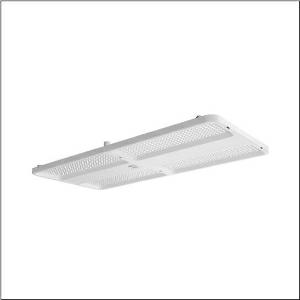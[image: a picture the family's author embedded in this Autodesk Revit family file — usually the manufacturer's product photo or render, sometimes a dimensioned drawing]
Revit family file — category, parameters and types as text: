
# Revit family: highbay_21_maxi_52hn12db4mda01
name_source: partatom
category: Lighting Fixtures
units: mm (PartAtom-declared; Revit-internal decimal feet)

## family parameters
Cut with Voids When Loaded = No
Host = Face
Light Source = No
Part Type = Normal
Room Calculation Point = No
Round Connector Dimension = Use Diameter
Shared = No

## types (1)
- --- (1 x LED, 28000 lm, 144.5 W, 4000K)
    Apparent Load = 144 VA
    CIE Flux Codes = 90 98 100 100 100
    Color Rendering = 80
    Color Temperature = 4000K
    Default Elevation = 1800 mm
    Description = high bay luminaire Highbay 21 maxi; direct symmetric wide distribution, light control with lens of PMMA; UGR ≤ 22 (X = 4H | Y = 8H | S = 0.25H | reflection values 70/50/20); luminous flux: 28.000lm; light colour: 840, colour temperature: 4000K, MacAdam ≤ 3 SDCM (initial), colour rendering: CRI > 80; luminous efficacy: 193,8lm/W; rated service life: 75.000h (L80) at AT= ta max; control: Bluetooth Mesh; for wireless networking: Node multi-sensor luminaire for setting up a local control solution without a higher-level application controller, intelligence completely integrated into the luminaire; with auto-swarm function: leading lighting creates safety. The function is already active without any „out-of-the-box“ commissioning; commissioning is not necessary thanks to „out-of-the-box“ functions: basic functions (presence lighting, follow-up times, fading times, etc.) are already preset at the factory; no control line such as DALI between the Node multi-sensor luminaires and Nodes is required, wireless integration of other Node luminaires and Node multi-sensor luminaires into the network is possible; number of Node multi-sensor luminaires in the project can be expanded as required, network sizes > 300 Nodes can be realized; can also be connected to lighting or building automation via various gateways upon request; integrated DALI2 ECG provides luminaire data (according to IEC62386, Part 251), energy data (Part 252), and monitoring and analytics data (Part 253) to higher-level systems for further processing; luminaire with PIR sensor (passive-infrared); with light sensor; luminaire connection: terminal, 5-pole, max. 2.5mm² (cable entry for one cable, Ø 8.5..16mm); mains connection: 230..240V, AC 50/60Hz; connected load: 144,5W; protection rating (complete): IP65; insulation class (complete): insulation class I (protective earthing); protection symbol: D; certification: CE, UKCA; internal wiring halogen-free; luminaire LABS conformity tested according to VDMA 24364:2018-05; Suitable for use in the food industry according to the specifications of IFS-Food, HACCP and/or BRC; housing frame of high-performance plastic PA6, matt traffic white (RAL 9016); cover of PMMA; dimension (LxWxH): 946 x 442 x 72mm; permissible operating ambient temperature: -20..+45°C (reducing of maximum allowable ambient temperature of 5°C with ceiling mounting); packaging unit: 1 piece; (delivery without accessories; please order mounting accessories separately)
    Height = 72 mm  [stored 0.23622 ft]
    Lamp = 1 x LED
    Lamp Light Flux = 28000 lm
    Lamp Power = 144.5 W
    Lamp count = 1
    Length = 946 mm
    Luminous efficacy = 194 lm/W
    Manufacturer = Siteco
    ModVariant = No
    Model = 52HN12DB4MDA01
    Mounting Place = Ceiling
    Mounting Type = Pendant
    Number of Poles = 1
    OnlyDefault = Yes
    Power Factor = 1
    Product Name = Highbay 21 maxi
    Product group = high bay luminaire
    ProductGroupID = 902
    Protection Class = Protection class I
    Protection Degree = IP 65
    RLX_Detail_Level = 1
    RLX_Emergency_Light_Flux = 0 lm
    RLX_Emergency_Type = 0
    RLX_Emergency_Type_DB = No
    RlxData = <blob elided: 128825 chars, md5=1e80c059>
    Socket = socket
    Standby Power = 0 W
    System Light Flux = 28000 lm
    System Power = 144 W
    Type Comments = factory setting: luminous flux: 100 % | dim-lin: 254 | 668 mA
    Type Image = l_1363267.jpg
    URL = http://relux.com
    VarID = @adj_012735
    Voltage = 0 V
    Weight = 0.00 kg
    Width = 442 mm

note: [stored X ft] marks values corroborated as IEEE doubles in the binary element streams (Revit-internal decimal feet)

## geometry (parser evidence)
native form markers: Blend x4, Sweep x9
no freeform markers — native parametric forms only
